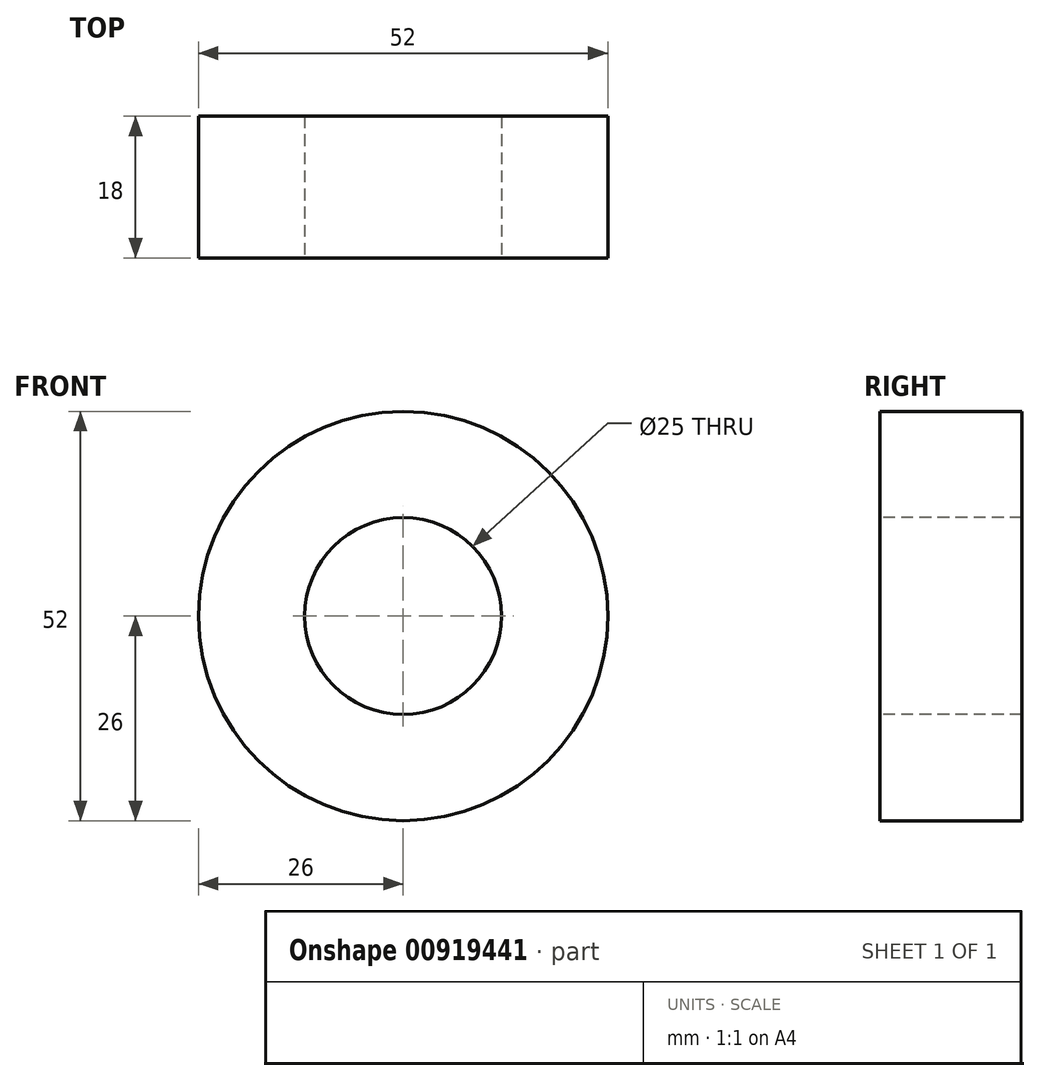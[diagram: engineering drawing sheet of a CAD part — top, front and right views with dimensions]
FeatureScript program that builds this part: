
annotation { "Feature Type Name" : "Feature", "Feature Type Description" : "" }
export const myFeature = defineFeature(function(context is Context, id is Id, definition is map)
    precondition{}
    {
        {
            var Q0;
            Q0=qCreatedBy(makeId("Right.planeOp"),FACE);
            var sketch = newSketch(context, id + "F0", { "sketchPlane" : qUnion([Q0])});
            skLineSegment(sketch, "E0", {"start": v(0, 21.32) * mm, "end": v(0, -17.75) * mm, "construction": true});
            skLineSegment(sketch, "E1.bottom", {"start": v(-9, 12.5) * mm, "end": v(9, 12.5) * mm});
            skLineSegment(sketch, "E1.top", {"start": v(-9, 26) * mm, "end": v(9, 26) * mm});
            skLineSegment(sketch, "E1.left", {"start": v(-9, 12.5) * mm, "end": v(-9, 26) * mm});
            skLineSegment(sketch, "E1.right", {"start": v(9, 12.5) * mm, "end": v(9, 26) * mm});
            skPoint(sketch, "E1.middle", {"position": v(0, 19.25) * mm});
            skLineSegment(sketch, "E2", {"start": v(-21.87, 0) * mm, "end": v(23.58, 0) * mm, "construction": true});
            skSolve(sketch);
        }
        {
            var Q0;
            Q0=makeQuery(id+"F0.imprint","IMPRINT",FACE,{"disambiguationData":[TD([[makeQuery(id+"F0.imprint","IMPRINT",EDGE,{"derivedFrom":sQuery(id+"F0.wireOp",EDGE,"E1.bottom")}),1.0]])]});
            var Q1;
            Q1=sQuery(id+"F0.wireOp",EDGE,"E2");
            revolve(context, id + "F1", {"surfaceOperationType" : NewSurfaceOperationType.NEW, "entities" : qUnion([Q0]), "axis" : qUnion([Q1]), "revolveType" : RevolveType.FULL});
        }
    });
